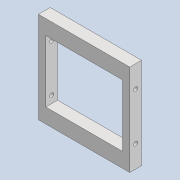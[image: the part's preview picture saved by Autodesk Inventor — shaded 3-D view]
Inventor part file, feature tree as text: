
AUTODESK INVENTOR PART (.ipt)
format: ipt  version: 2020 (Build 240168000, 168)  size: 99,328 bytes
history: native  units: mm
features: reference x10, other x4, extrude x2, sketch x2
ambient origin geometry x8: Origin, YZ Plane, XZ Plane, XY Plane, X Axis, Y Axis, Z Axis, Center Point
bodies: Solid1 (feature_tree)
feature tree (18):
  extrude  "Extrusion1"  Depth=21.0mm
  extrude  "Extrusion2"  Depth=2.5mm
  sketch  "Sketch1"  dims[d0=26.0mm d1=21.0mm]
  reference  "Reference1"
  reference  "Reference2"
  reference  "Reference3"
  reference  "Reference4"
  reference  "Reference5"
  reference  "Reference6"
  reference  "Reference7"
  reference  "Reference8"
  sketch  "Sketch2"  dims[d2=5.0mm d3=2.5mm d4=4.0mm d5=0.0mm d6=4.0mm d7=0.0mm]
  reference  "Reference9"
  reference  "Reference10"
  parser-record x1  (decoder bookkeeping rows leaked as tree rows — omitted from the tree; the rows remain in map.json)
  other  "tip_3_n_ass.iam"
  other  "bearing_hh_1:2"
  other  "bearing_hh_1:1"
note: 1 file-system path scrubbed to <path> (originals preserved in map.json)
